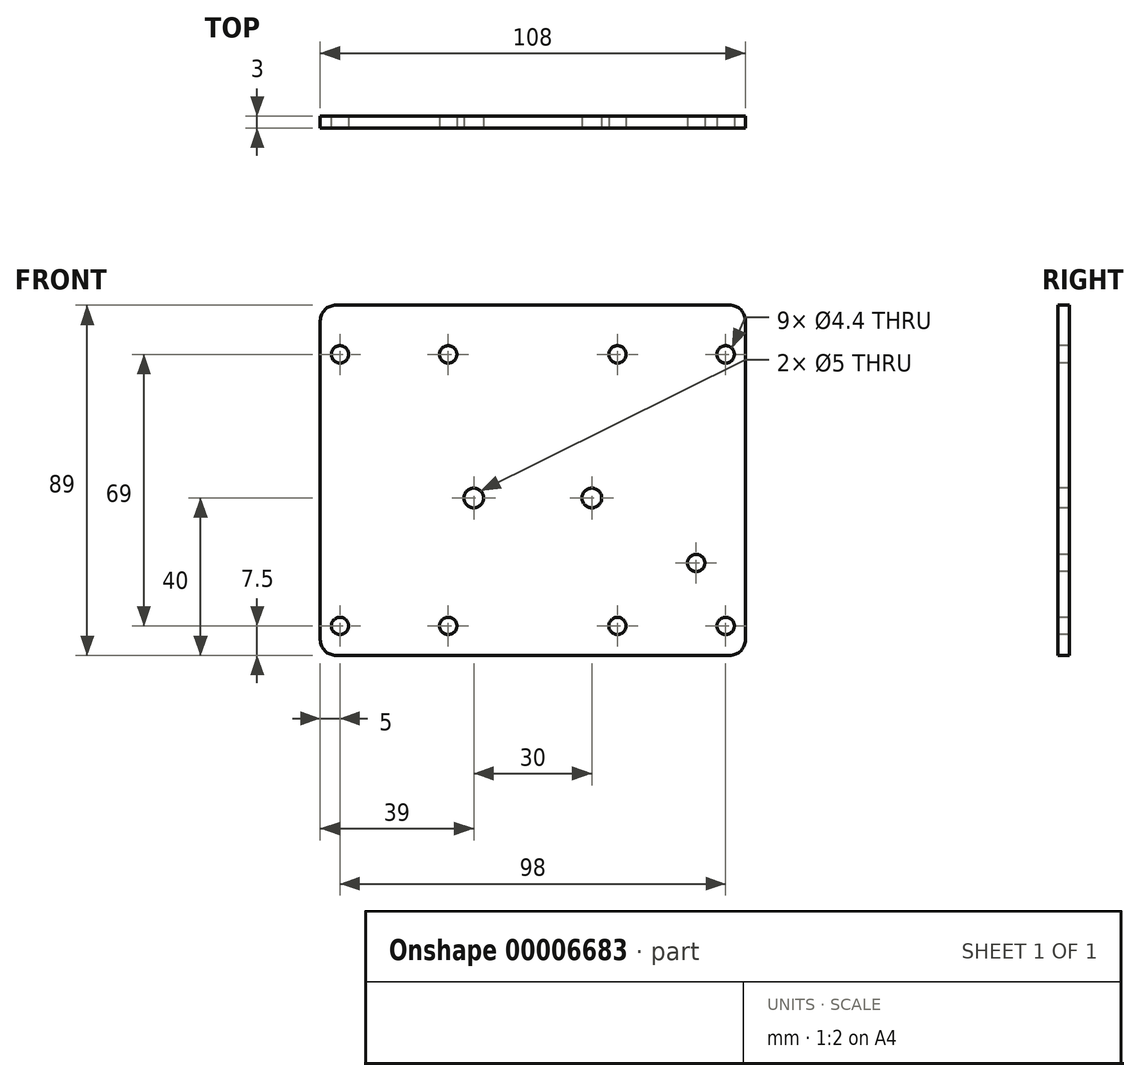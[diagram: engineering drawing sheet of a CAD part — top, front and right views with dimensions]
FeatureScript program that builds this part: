
annotation { "Feature Type Name" : "Feature", "Feature Type Description" : "" }
export const myFeature = defineFeature(function(context is Context, id is Id, definition is map)
    precondition{}
    {
        {
            var Q0;
            Q0=qCreatedBy(makeId("Front.planeOp"),FACE);
            var sketch = newSketch(context, id + "F0", { "sketchPlane" : qUnion([Q0])});
            skLineSegment(sketch, "E0.bottom", {"start": v(4, 0) * mm, "end": v(104, 0) * mm});
            skLineSegment(sketch, "E0.top", {"start": v(4, 89) * mm, "end": v(104, 89) * mm});
            skLineSegment(sketch, "E0.left", {"start": v(0, 4) * mm, "end": v(0, 85) * mm});
            skLineSegment(sketch, "E0.right", {"start": v(108, 4) * mm, "end": v(108, 85) * mm});
            skPoint(sketch, "E1.visualSharp", {"position": v(0, 89) * mm});
            skArc(sketch, "E1.filletArc", {"start": v(4, 89) * mm, "mid": v(1.17, 87.83) * mm, "end": v(0, 85) * mm});
            skPoint(sketch, "E2.visualSharp", {"position": v(108, 89) * mm});
            skArc(sketch, "E2.filletArc", {"start": v(108, 85) * mm, "mid": v(106.83, 87.83) * mm, "end": v(104, 89) * mm});
            skPoint(sketch, "E3.visualSharp", {"position": v(108, 0) * mm});
            skArc(sketch, "E3.filletArc", {"start": v(104, 0) * mm, "mid": v(106.83, 1.17) * mm, "end": v(108, 4) * mm});
            skPoint(sketch, "E4.visualSharp", {"position": v(0, 0) * mm});
            skArc(sketch, "E4.filletArc", {"start": v(0, 4) * mm, "mid": v(1.17, 1.17) * mm, "end": v(4, 0) * mm});
            skSolve(sketch);
        }
        {
            var Q0;
            Q0 = qSketchRegion(id + "F0", true);
            extrude(context, id + "F1", {"entities" : qUnion([Q0]), "depth" : 3 * mm});
        }
        {
            var Q0;
            Q0=makeQuery(id+"F1.opExtrude","CAP_FACE",FACE,{"disambiguationData":[OSD([sQuery(id+"F0.wireOp",EDGE,"E0.bottom"),sQuery(id+"F0.wireOp",EDGE,"E0.top"),sQuery(id+"F0.wireOp",EDGE,"E0.left"),sQuery(id+"F0.wireOp",EDGE,"E0.right"),sQuery(id+"F0.wireOp",EDGE,"E1.filletArc"),sQuery(id+"F0.wireOp",EDGE,"E2.filletArc"),sQuery(id+"F0.wireOp",EDGE,"E3.filletArc"),sQuery(id+"F0.wireOp",EDGE,"E4.filletArc")])],"isStart":false});
            var sketch = newSketch(context, id + "F2", { "sketchPlane" : qUnion([Q0])});
            skCircle(sketch, "E5", {"center": v(5, 76.5) * mm, "radius": 2.2 * mm});
            skCircle(sketch, "E6", {"center": v(32.5, 76.5) * mm, "radius": 2.2 * mm});
            skCircle(sketch, "E7", {"center": v(75.5, 76.5) * mm, "radius": 2.2 * mm});
            skCircle(sketch, "E8", {"center": v(103, 76.5) * mm, "radius": 2.2 * mm});
            skCircle(sketch, "E9", {"center": v(5, 7.5) * mm, "radius": 2.2 * mm});
            skCircle(sketch, "E10", {"center": v(32.5, 7.5) * mm, "radius": 2.2 * mm});
            skCircle(sketch, "E11", {"center": v(75.5, 7.5) * mm, "radius": 2.2 * mm});
            skCircle(sketch, "E12", {"center": v(103, 7.5) * mm, "radius": 2.2 * mm});
            skCircle(sketch, "E13", {"center": v(95.5, 23.5) * mm, "radius": 2.2 * mm});
            skSolve(sketch);
        }
        {
            var Q0;
            Q0 = qSketchRegion(id + "F2", true);
            extrude(context, id + "F3", {"entities" : qUnion([Q0]), "operationType" : NewBodyOperationType.REMOVE, "endBound" : BoundingType.THROUGH_ALL, "oppositeDirection" : true, "depth" : 25 * mm});
        }
        {
            var Q0;
            Q0=makeQuery(id+"F1.opExtrude","CAP_FACE",FACE,{"disambiguationData":[OSD([sQuery(id+"F0.wireOp",EDGE,"E0.bottom"),sQuery(id+"F0.wireOp",EDGE,"E0.top"),sQuery(id+"F0.wireOp",EDGE,"E0.left"),sQuery(id+"F0.wireOp",EDGE,"E0.right"),sQuery(id+"F0.wireOp",EDGE,"E1.filletArc"),sQuery(id+"F0.wireOp",EDGE,"E2.filletArc"),sQuery(id+"F0.wireOp",EDGE,"E3.filletArc"),sQuery(id+"F0.wireOp",EDGE,"E4.filletArc")])],"isStart":false});
            var sketch = newSketch(context, id + "F4", { "sketchPlane" : qUnion([Q0])});
            skCircle(sketch, "E14", {"center": v(39, 40) * mm, "radius": 2.5 * mm});
            skCircle(sketch, "E15", {"center": v(69, 40) * mm, "radius": 2.5 * mm});
            skSolve(sketch);
        }
        {
            var Q0;
            Q0 = qSketchRegion(id + "F4", true);
            extrude(context, id + "F5", {"entities" : qUnion([Q0]), "operationType" : NewBodyOperationType.REMOVE, "endBound" : BoundingType.THROUGH_ALL, "oppositeDirection" : true, "depth" : 25 * mm});
        }
    });
